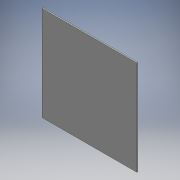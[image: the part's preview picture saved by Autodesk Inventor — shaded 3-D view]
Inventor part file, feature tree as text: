
AUTODESK INVENTOR PART (.ipt)
format: ipt  version: 2016 (Build 200138000, 138)  size: 84,992 bytes
history: native  units: mm
features: other x1, extrude x1, sketch x1
ambient origin geometry x8: Origin, YZ Plane, XZ Plane, XY Plane, X Axis, Y Axis, Z Axis, Center Point
bodies: Body1 (feature_tree)
feature tree (3):
  other  "ソリッド1"
  extrude  "押し出し1"  Depth=200.0mm
  sketch  "スケッチ1"
